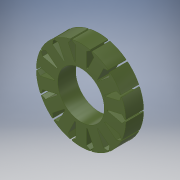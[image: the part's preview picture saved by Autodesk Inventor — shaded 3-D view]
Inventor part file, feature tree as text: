
AUTODESK INVENTOR PART (.ipt)
format: ipt  version: 2019.4 (Build 234330000, 330)  size: 242,176 bytes
history: native  units: mm
features: extrude x3, sketch x3, mirror x1, pattern_circular x1
ambient origin geometry x8: Origin, YZ Plane, XZ Plane, XY Plane, X Axis, Y Axis, Z Axis, Center Point
bodies: Solid1 (feature_tree)
feature tree (8):
  extrude  "Extrusion1"  Depth=30.0mm
  extrude  "Extrusion2"  Depth=10.0mm
  mirror  "Mirror1"
  pattern_circular  "Circular Pattern1"  [2 undecoded]
  extrude  "Extrusion3"  Depth=6.0mm
  sketch  "Sketch1"  dims[d0=50.0mm d1=30.0mm]
  sketch  "Sketch2"  dims[d2=8.0mm d3=4.0mm d4=10.0mm d5=5.0mm]
  sketch  "Sketch3"  dims[d6=2.0mm d7=10.0mm d8=0.0mm d9=6.0mm d10=3.0mm d11=0.5mm d12=10.0mm d13=0.0mm d14=140.0mm d15=360.0deg d17=26.0mm d18=10.0mm d19=0.0mm]
note: 2 required parameter values undecoded (feature->parameter linkage not recoverable at this tier; creation-order binding heuristic only, values carry confidence <= 0.55)
